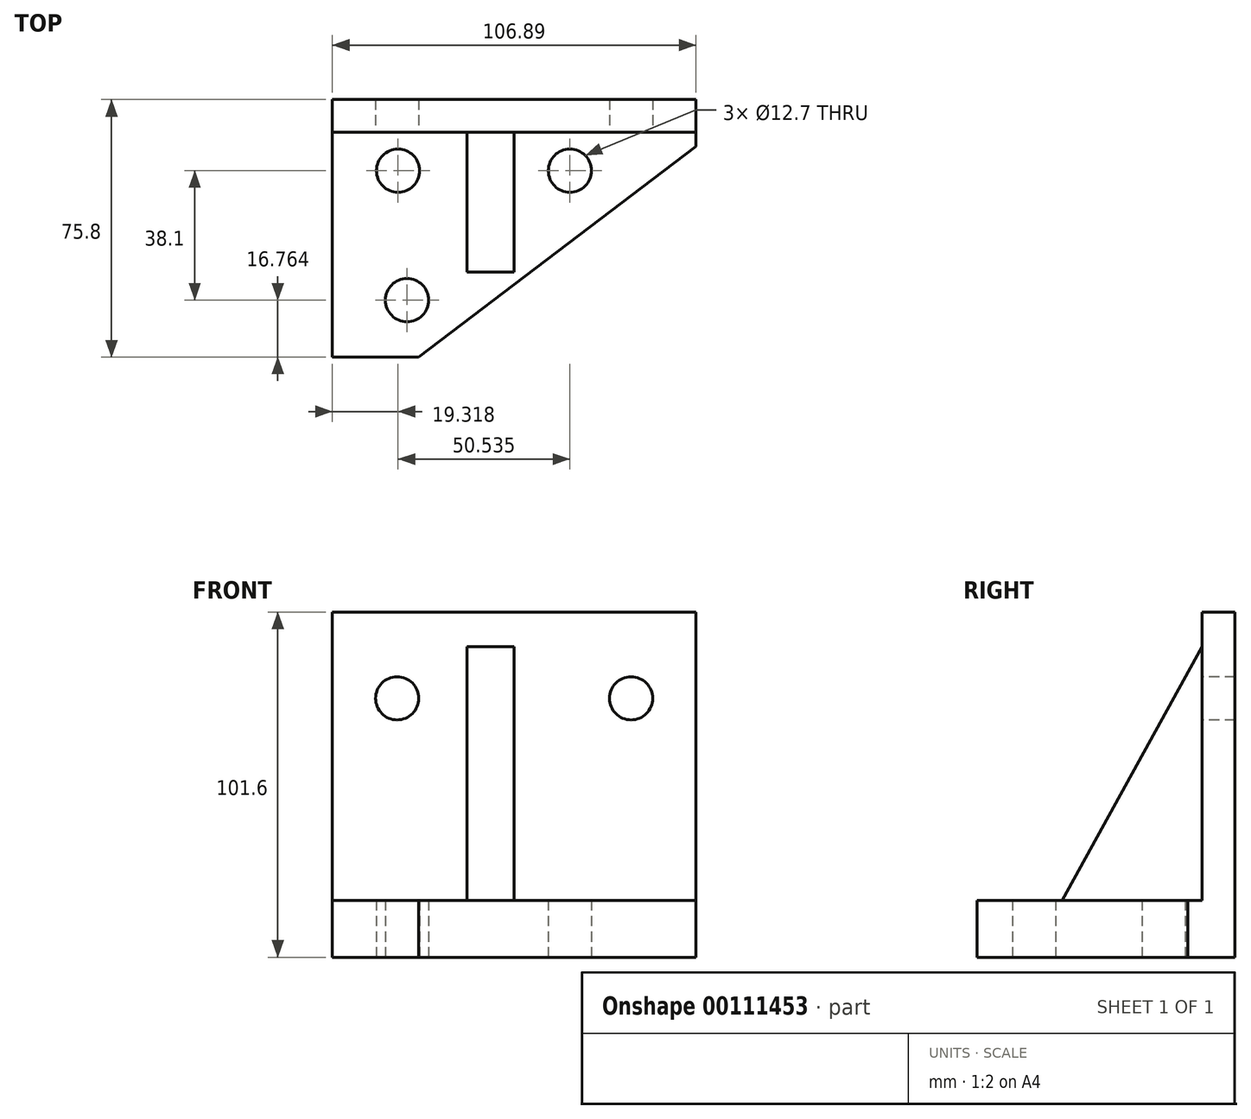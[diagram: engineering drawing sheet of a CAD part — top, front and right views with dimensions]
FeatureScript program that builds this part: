
annotation { "Feature Type Name" : "Feature", "Feature Type Description" : "" }
export const myFeature = defineFeature(function(context is Context, id is Id, definition is map)
    precondition{}
    {
        {
            var Q0;
            Q0=qCreatedBy(makeId("Top.planeOp"),FACE);
            var sketch = newSketch(context, id + "F0", { "sketchPlane" : qUnion([Q0])});
            skLineSegment(sketch, "E0", {"start": v(-48.82, 0) * mm, "end": v(58.07, 0) * mm});
            skLineSegment(sketch, "E1", {"start": v(58.07, 0) * mm, "end": v(58.07, -10.05) * mm});
            skLineSegment(sketch, "E2", {"start": v(58.07, -10.05) * mm, "end": v(-48.82, -10.05) * mm});
            skLineSegment(sketch, "E3", {"start": v(-48.82, -10.05) * mm, "end": v(-48.82, 0) * mm});
            skLineSegment(sketch, "E4", {"start": v(-48.82, -10.05) * mm, "end": v(-48.82, -76.2) * mm});
            skLineSegment(sketch, "E5", {"start": v(-48.82, -76.2) * mm, "end": v(-23.42, -76.2) * mm});
            skLineSegment(sketch, "E6", {"start": v(-23.42, -76.2) * mm, "end": v(58.07, -14.22) * mm});
            skLineSegment(sketch, "E7", {"start": v(58.07, -14.22) * mm, "end": v(58.07, -10.05) * mm});
            skLineSegment(sketch, "E8", {"start": v(-9.2, -10.05) * mm, "end": v(-9.2, -50.8) * mm, "construction": true});
            skLineSegment(sketch, "E9", {"start": v(-9.2, -50.8) * mm, "end": v(0.03, -50.8) * mm, "construction": true});
            skLineSegment(sketch, "E10", {"start": v(0.03, -50.8) * mm, "end": v(0.03, -10.05) * mm, "construction": true});
            skCircle(sketch, "E11", {"center": v(-26.86, -59.44) * mm, "radius": 6.35 * mm});
            skCircle(sketch, "E12", {"center": v(-29.5, -21.34) * mm, "radius": 6.35 * mm});
            skCircle(sketch, "E13", {"center": v(21.03, -21.34) * mm, "radius": 6.35 * mm});
            skSolve(sketch);
        }
        {
            var Q0;
            Q0=makeQuery(id+"F0.imprint","IMPRINT",FACE,{"disambiguationData":[TD([[makeQuery(id+"F0.imprint","IMPRINT",EDGE,{"derivedFrom":sQuery(id+"F0.wireOp",EDGE,"E2")}),1.0]])]});
            extrude(context, id + "F1", {"entities" : qUnion([Q0]), "depth" : 16.76 * mm});
        }
        {
            var Q0;
            Q0=makeQuery(id+"F1.opExtrude","SWEPT_FACE",FACE,{"disambiguationData":[OSD([sQuery(id+"F0.wireOp",EDGE,"E2")])]});
            var sketch = newSketch(context, id + "F2", { "sketchPlane" : qUnion([Q0])});
            skLineSegment(sketch, "E14", {"start": v(-58.07, 0) * mm, "end": v(48.82, 0) * mm});
            skLineSegment(sketch, "E15", {"start": v(48.82, 0) * mm, "end": v(48.82, 101.6) * mm});
            skLineSegment(sketch, "E16", {"start": v(48.82, 101.6) * mm, "end": v(-58.07, 101.6) * mm});
            skLineSegment(sketch, "E17", {"start": v(-58.07, 101.6) * mm, "end": v(-58.07, 0) * mm});
            skCircle(sketch, "E18", {"center": v(-39.02, 76.2) * mm, "radius": 6.35 * mm});
            skCircle(sketch, "E19", {"center": v(29.77, 76.2) * mm, "radius": 6.35 * mm});
            skLineSegment(sketch, "E20", {"start": v(9.2, 16.76) * mm, "end": v(-18.45, 16.76) * mm});
            skLineSegment(sketch, "E21", {"start": v(-18.45, 16.76) * mm, "end": v(-18.45, 88.9) * mm});
            skLineSegment(sketch, "E22", {"start": v(-18.45, 88.9) * mm, "end": v(9.2, 88.9) * mm});
            skLineSegment(sketch, "E23", {"start": v(9.2, 88.9) * mm, "end": v(9.2, 16.76) * mm});
            skSolve(sketch);
        }
        {
            var Q0;
            {var subQ0=sQuery(id+"F2.wireOp",EDGE,"E14");Q0=makeQuery(id+"F2.imprint","IMPRINT",FACE,{"disambiguationData":[TD([[makeQuery(id+"F2.imprint","IMPRINT",EDGE,{"derivedFrom":subQ0}),1.0]])]});}
            var Q1;
            {var subQ5=sQuery(id+"F2.wireOp",EDGE,"E16");Q1=makeQuery(id+"F2.imprint","IMPRINT",FACE,{"disambiguationData":[TD([[makeQuery(id+"F2.imprint","IMPRINT",EDGE,{"derivedFrom":subQ5}),1.0]])]});}
            var Q2;
            Q2=makeQuery(id+"F2.imprint","IMPRINT",FACE,{"disambiguationData":[TD([[makeQuery(id+"F2.imprint","IMPRINT",EDGE,{"derivedFrom":sQuery(id+"F2.wireOp",EDGE,"E20")}),1.0]])]});
            extrude(context, id + "F3", {"entities" : qUnion([Q0, Q1, Q2]), "operationType" : NewBodyOperationType.ADD, "depth" : 9.65 * mm});
        }
        {
            var Q0;
            Q0=makeQuery(id+"F1.opExtrude","CAP_FACE",FACE,{"disambiguationData":[OSD([sQuery(id+"F0.wireOp",EDGE,"E2"),sQuery(id+"F0.wireOp",EDGE,"E4"),sQuery(id+"F0.wireOp",EDGE,"E5"),sQuery(id+"F0.wireOp",EDGE,"E6"),sQuery(id+"F0.wireOp",EDGE,"E7"),sQuery(id+"F0.wireOp",EDGE,"E11"),sQuery(id+"F0.wireOp",EDGE,"E12"),sQuery(id+"F0.wireOp",EDGE,"E13")])],"isStart":false});
            var sketch = newSketch(context, id + "F4", { "sketchPlane" : qUnion([Q0])});
            skLineSegment(sketch, "E24", {"start": v(-48.82, -51.2) * mm, "end": v(-9.2, -51.2) * mm});
            skLineSegment(sketch, "E25.bottom", {"start": v(-9.2, -51.2) * mm, "end": v(4.63, -51.2) * mm});
            skLineSegment(sketch, "E25.top", {"start": v(-9.2, -10.05) * mm, "end": v(4.63, -10.05) * mm});
            skLineSegment(sketch, "E25.left", {"start": v(-9.2, -51.2) * mm, "end": v(-9.2, -10.05) * mm});
            skLineSegment(sketch, "E25.right", {"start": v(4.63, -51.2) * mm, "end": v(4.63, -10.05) * mm});
            skSolve(sketch);
        }
        {
            var Q0;
            Q0=makeQuery(id+"F4.imprint","IMPRINT",FACE,{"disambiguationData":[TD([[makeQuery(id+"F4.imprint","IMPRINT",EDGE,{"derivedFrom":sQuery(id+"F4.wireOp",EDGE,"E25.bottom")}),1.0]])]});
            extrude(context, id + "F5", {"entities" : qUnion([Q0]), "operationType" : NewBodyOperationType.ADD, "depth" : 74.68 * mm});
        }
        {
            var Q0;
            Q0=makeQuery(id+"F5.opExtrude","SWEPT_FACE",FACE,{"disambiguationData":[OSD([sQuery(id+"F4.wireOp",EDGE,"E25.right")])]});
            var sketch = newSketch(context, id + "F6", { "sketchPlane" : qUnion([Q0])});
            skLineSegment(sketch, "E26", {"start": v(-51.2, 16.76) * mm, "end": v(-10.05, 91.44) * mm});
            skSolve(sketch);
        }
        {
            var Q0;
            Q0 = qSketchRegion(id + "F6", true);
            var Q1;
            Q1=makeQuery(id+"F6.imprint","IMPRINT",FACE,{"disambiguationData":[TD([[makeQuery(id+"F6.imprint","IMPRINT",EDGE,{"derivedFrom":sQuery(id+"F6.wireOp",EDGE,"E26")}),1.0]])]});
            extrude(context, id + "F7", {"entities" : qUnion([Q0, Q1]), "operationType" : NewBodyOperationType.REMOVE, "oppositeDirection" : true, "depth" : 53.05 * mm});
        }
    });
